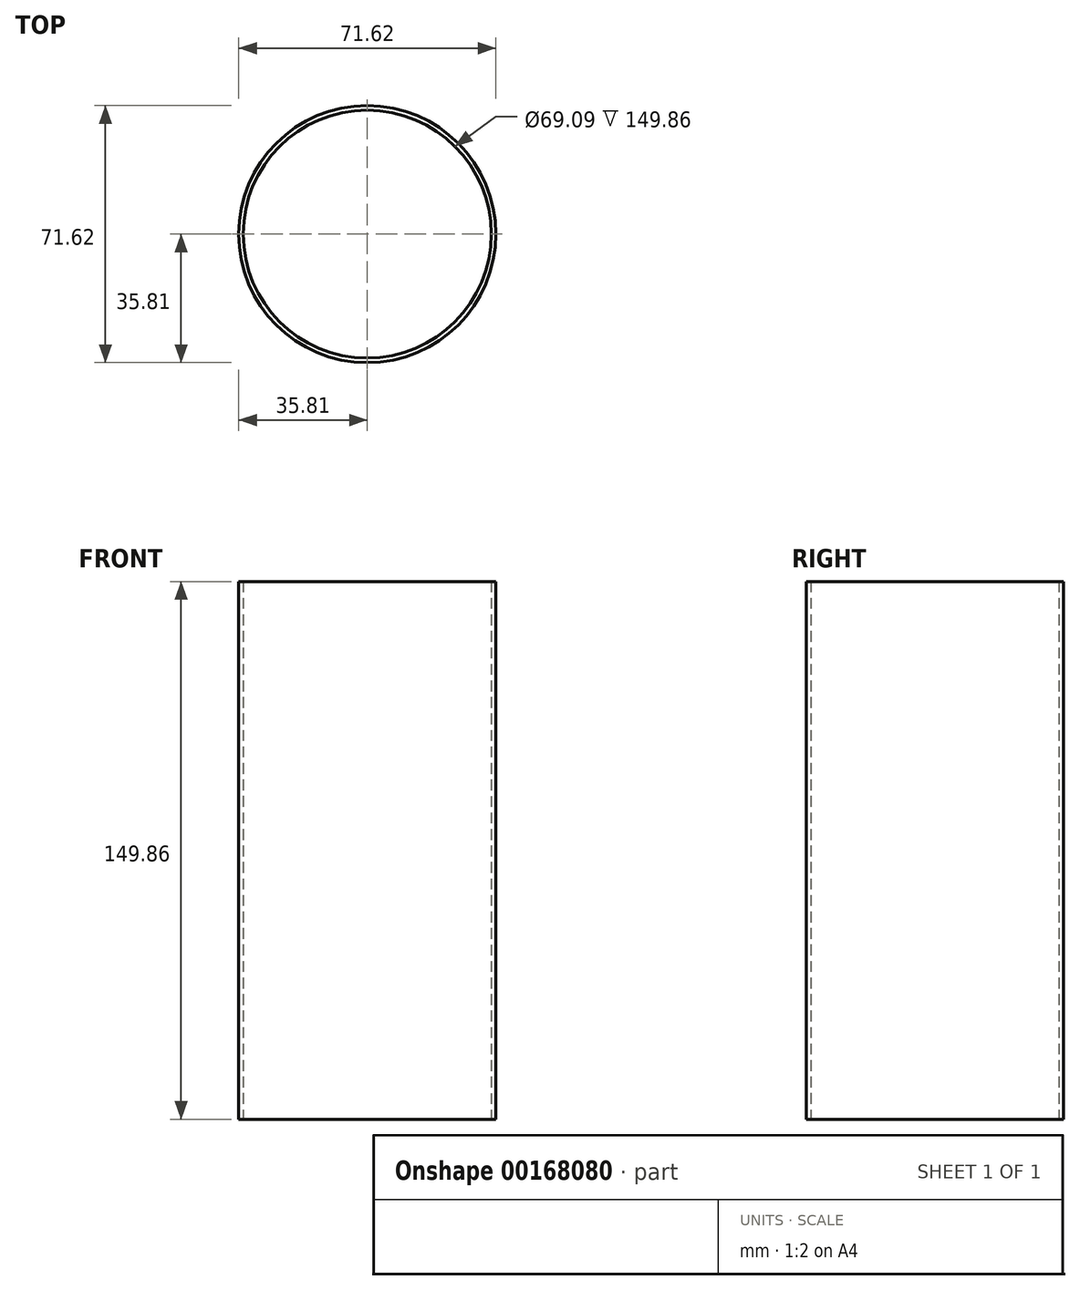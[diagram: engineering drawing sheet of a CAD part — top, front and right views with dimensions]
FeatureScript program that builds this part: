
annotation { "Feature Type Name" : "Feature", "Feature Type Description" : "" }
export const myFeature = defineFeature(function(context is Context, id is Id, definition is map)
    precondition{}
    {
        {
            var Q0;
            Q0=qCreatedBy(makeId("Top.planeOp"),FACE);
            var sketch = newSketch(context, id + "F0", { "sketchPlane" : qUnion([Q0])});
            skCircle(sketch, "E0", {"center": v(0, 0) * mm, "radius": 35.81 * mm});
            skCircle(sketch, "E1", {"center": v(0, 0) * mm, "radius": 34.54 * mm});
            skSolve(sketch);
        }
        {
            var Q0;
            Q0 = qSketchRegion(id + "F0", true);
            extrude(context, id + "F1", {"entities" : qUnion([Q0]), "depth" : 149.86 * mm});
        }
    });
